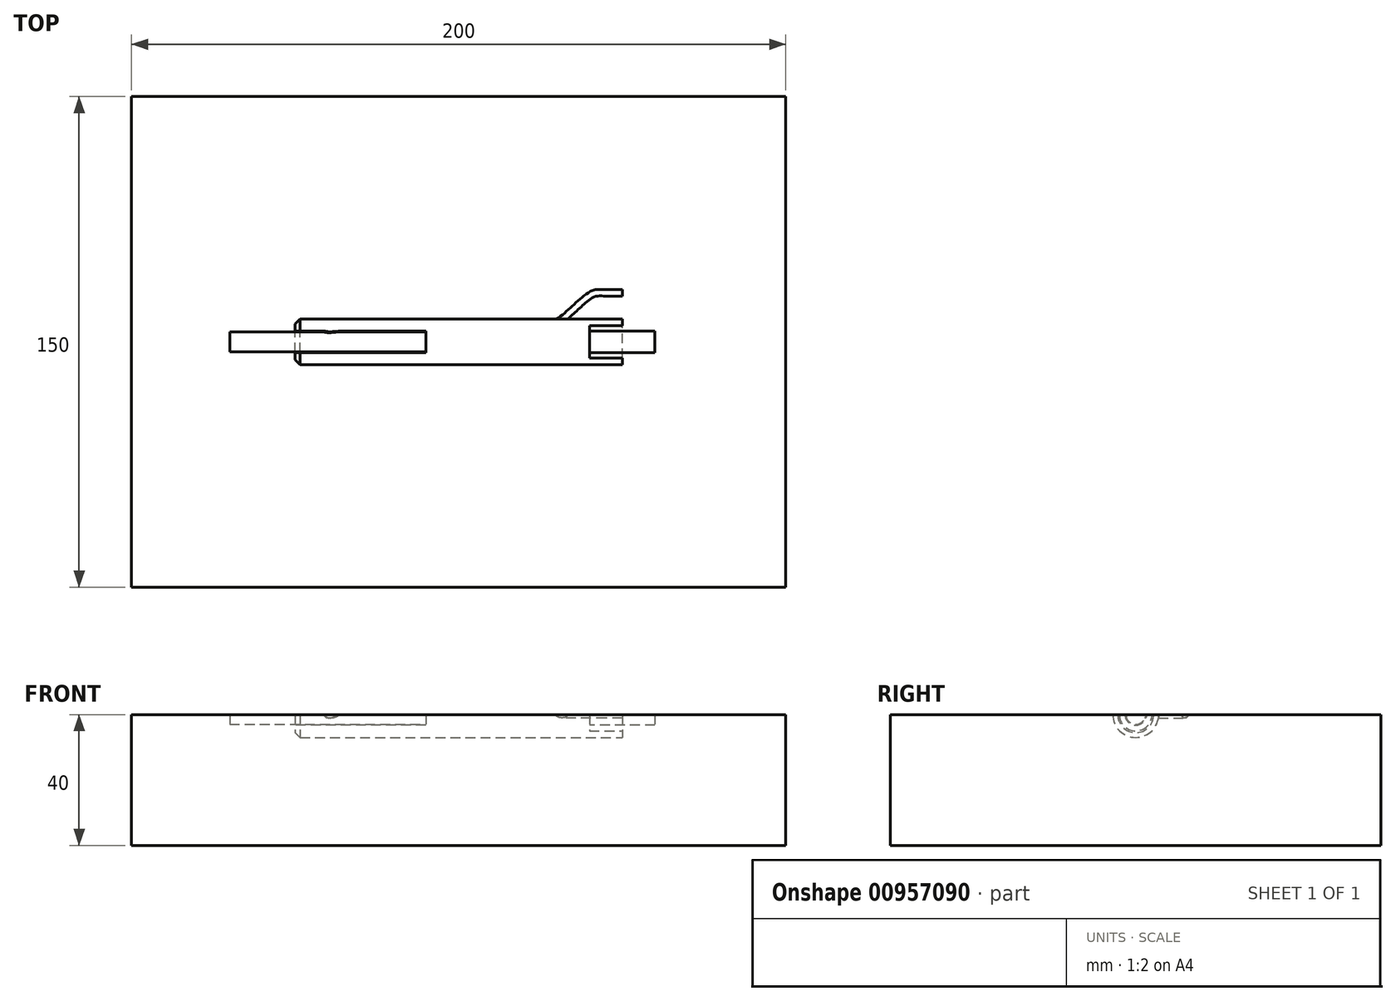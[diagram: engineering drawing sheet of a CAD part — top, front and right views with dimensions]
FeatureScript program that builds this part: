
annotation { "Feature Type Name" : "Feature", "Feature Type Description" : "" }
export const myFeature = defineFeature(function(context is Context, id is Id, definition is map)
    precondition{}
    {
        {
            var Q0;
            Q0=qCreatedBy(makeId("Top.planeOp"),FACE);
            var sketch = newSketch(context, id + "F0", { "sketchPlane" : qUnion([Q0])});
            skLineSegment(sketch, "E0.bottom", {"start": v(-100, 75) * mm, "end": v(100, 75) * mm});
            skLineSegment(sketch, "E0.top", {"start": v(-100, -75) * mm, "end": v(100, -75) * mm});
            skLineSegment(sketch, "E0.left", {"start": v(-100, 75) * mm, "end": v(-100, -75) * mm});
            skLineSegment(sketch, "E0.right", {"start": v(100, 75) * mm, "end": v(100, -75) * mm});
            skSolve(sketch);
        }
        {
            var Q0;
            Q0=makeQuery(id+"F0.imprint","IMPRINT",FACE,{"disambiguationData":[TD([[makeQuery(id+"F0.imprint","IMPRINT",EDGE,{"derivedFrom":sQuery(id+"F0.wireOp",EDGE,"E0.bottom")}),-1.0]])]});
            extrude(context, id + "F1", {"entities" : qUnion([Q0]), "oppositeDirection" : true, "depth" : 40 * mm, "offsetDistance" : 25 * mm});
        }
        {
            var Q0;
            Q0=qCreatedBy(makeId("Right.planeOp"),FACE);
            var sketch = newSketch(context, id + "F2", { "sketchPlane" : qUnion([Q0])});
            skArc(sketch, "E1", {"start": v(-7, 0) * mm, "mid": v(0, -7) * mm, "end": v(7, 0) * mm});
            skLineSegment(sketch, "E2.0.0", {"start": v(75, 0) * mm, "end": v(-75, 0) * mm});
            skLineSegment(sketch, "E2.0.2", {"start": v(-75, 0) * mm, "end": v(75, 0) * mm, "construction": true});
            skLineSegment(sketch, "E3", {"start": v(7, 0) * mm, "end": v(-7, 0) * mm});
            skSolve(sketch);
        }
        {
            var Q0;
            Q0 = qSketchRegion(id + "F2", true);
            extrude(context, id + "F3", {"entities" : qUnion([Q0]), "operationType" : NewBodyOperationType.REMOVE, "endBound" : BoundingType.SYMMETRIC, "oppositeDirection" : true, "depth" : 100 * mm, "offsetDistance" : 25 * mm});
        }
        {
            var Q0;
            Q0=makeQuery(id+"F3.boolean.opBoolean","COPY",FACE,{"derivedFrom":makeQuery(id+"F3.opExtrude","CAP_FACE",FACE,{"disambiguationData":[OSD([sQuery(id+"F2.wireOp",EDGE,"E1"),sQuery(id+"F2.wireOp",EDGE,"E3")])],"isStart":true})});
            var sketch = newSketch(context, id + "F4", { "sketchPlane" : qUnion([Q0])});
            skPoint(sketch, "E4.0", {"position": v(0, 0) * mm});
            skArc(sketch, "E5", {"start": v(-5, 0) * mm, "mid": v(0, -5) * mm, "end": v(5, 0) * mm});
            skLineSegment(sketch, "E6", {"start": v(-5, 0) * mm, "end": v(5, 0) * mm});
            skSolve(sketch);
        }
        {
            var Q0;
            Q0=makeQuery(id+"F4.imprint","IMPRINT",FACE,{"disambiguationData":[TD([[makeQuery(id+"F4.imprint","IMPRINT",EDGE,{"derivedFrom":sQuery(id+"F4.wireOp",EDGE,"E5")}),1.0]])]});
            extrude(context, id + "F5", {"entities" : qUnion([Q0]), "operationType" : NewBodyOperationType.ADD, "depth" : 10 * mm, "offsetDistance" : 25 * mm});
        }
        {
            var Q0;
            Q0=makeQuery(id+"F5.opExtrude","CAP_FACE",FACE,{"disambiguationData":[OSD([sQuery(id+"F4.wireOp",EDGE,"E5"),sQuery(id+"F4.wireOp",EDGE,"E6")])],"isStart":false});
            var sketch = newSketch(context, id + "F6", { "sketchPlane" : qUnion([Q0])});
            skCircle(sketch, "E7", {"center": v(0, 0) * mm, "radius": 3.25 * mm});
            skSolve(sketch);
        }
        {
            var Q0;
            {var subQ0=sQuery(id+"F6.wireOp",EDGE,"E7");var subQ1=makeQuery(id+"F5.opExtrude","CAP_EDGE",EDGE,{"disambiguationData":[OSD([sQuery(id+"F4.wireOp",EDGE,"E6")])],"isStart":false});var subQ2=makeQuery(id+"F6.imprint","INTERSECT",VERTEX,{"disambiguationData":[OD(0.0)],"derivedFrom":[subQ1,subQ0]});Q0=makeQuery(id+"F6.imprint","IMPRINT",FACE,{"disambiguationData":[TD([[makeQuery(id+"F6.imprint","IMPRINT",EDGE,{"disambiguationData":[TD([[subQ2,1.0]])],"derivedFrom":subQ0}),1.0]])]});}
            var Q1;
            {var subQ0=sQuery(id+"F6.wireOp",EDGE,"E7");var subQ1=makeQuery(id+"F5.opExtrude","CAP_EDGE",EDGE,{"disambiguationData":[OSD([sQuery(id+"F4.wireOp",EDGE,"E6")])],"isStart":false});var subQ2=makeQuery(id+"F6.imprint","INTERSECT",VERTEX,{"disambiguationData":[OD(0.0)],"derivedFrom":[subQ1,subQ0]});Q1=makeQuery(id+"F6.imprint","IMPRINT",FACE,{"disambiguationData":[TD([[makeQuery(id+"F6.imprint","IMPRINT",EDGE,{"disambiguationData":[TD([[subQ2,-1.0]])],"derivedFrom":subQ0}),1.0]])]});}
            extrude(context, id + "F7", {"entities" : qUnion([Q0, Q1]), "operationType" : NewBodyOperationType.REMOVE, "oppositeDirection" : true, "depth" : 20 * mm, "offsetDistance" : 25 * mm});
        }
        {
            var Q0;
            Q0=makeQuery(id+"F3.boolean.opBoolean","COPY",FACE,{"derivedFrom":makeQuery(id+"F3.opExtrude","CAP_FACE",FACE,{"disambiguationData":[OSD([sQuery(id+"F2.wireOp",EDGE,"E1"),sQuery(id+"F2.wireOp",EDGE,"E3")])],"isStart":false})});
            var sketch = newSketch(context, id + "F8", { "sketchPlane" : qUnion([Q0])});
            skArc(sketch, "E8", {"start": v(-3.25, 0) * mm, "mid": v(0, -3.25) * mm, "end": v(3.25, 0) * mm});
            skLineSegment(sketch, "E9", {"start": v(-3.25, 0) * mm, "end": v(3.25, 0) * mm});
            skSolve(sketch);
        }
        {
            var Q0;
            Q0 = qSketchRegion(id + "F8", true);
            extrude(context, id + "F9", {"entities" : qUnion([Q0]), "operationType" : NewBodyOperationType.ADD, "depth" : 40 * mm, "offsetDistance" : 25 * mm});
        }
        {
            var Q0;
            Q0=makeQuery(id+"F3.boolean.opBoolean","COPY",EDGE,{"derivedFrom":makeQuery(id+"F3.opExtrude","CAP_EDGE",EDGE,{"disambiguationData":[OSD([sQuery(id+"F2.wireOp",EDGE,"E1")])],"isStart":false})});
            chamfer(context, id + "F10", {"entities" : qUnion([Q0]), "width" : 1.5 * mm, "tangentPropagation" : true});
        }
        {
            var Q0;
            Q0=makeQuery(id+"F1.opExtrude","CAP_FACE",FACE,{"disambiguationData":[OSD([sQuery(id+"F0.wireOp",EDGE,"E0.bottom"),sQuery(id+"F0.wireOp",EDGE,"E0.top"),sQuery(id+"F0.wireOp",EDGE,"E0.left"),sQuery(id+"F0.wireOp",EDGE,"E0.right")])],"isStart":true});
            var sketch = newSketch(context, id + "F11", { "sketchPlane" : qUnion([Q0])});
            skLineSegment(sketch, "E10.0", {"start": v(50, -5) * mm, "end": v(50, -7) * mm});
            skLineSegment(sketch, "E11.0.0", {"start": v(-100, 75) * mm, "end": v(-100, -75) * mm});
            skLineSegment(sketch, "E11.0.1", {"start": v(-100, -75) * mm, "end": v(100, -75) * mm});
            skLineSegment(sketch, "E11.0.2", {"start": v(100, -75) * mm, "end": v(100, 75) * mm});
            skLineSegment(sketch, "E11.0.3", {"start": v(100, 75) * mm, "end": v(-100, 75) * mm});
            skLineSegment(sketch, "E12", {"start": v(50, 15) * mm, "end": v(45, 15) * mm});
            skFitSpline(sketch, "E13", {"points": [v(45, 15) * mm, v(40.7, 14.52) * mm, v(31.65, 7) * mm, v(21.87, 5) * mm, v(-30.52, 5) * mm, v(-43.04, 0) * mm], "startDerivative": vector(-47.27, 0) * mm, "endDerivative": vector(-74.54, -70.61) * mm});
            skLineSegment(sketch, "E14.0.1", {"start": v(50, 7) * mm, "end": v(-50, 7) * mm});
            skLineSegment(sketch, "E14.0.2", {"start": v(-50, -7) * mm, "end": v(-50, 7) * mm});
            skLineSegment(sketch, "E14.0.3", {"start": v(-50, -7) * mm, "end": v(50, -7) * mm});
            skSolve(sketch);
        }
        {
            var Q0;
            Q0=makeQuery(id+"F3.boolean.opBoolean","COPY",FACE,{"derivedFrom":makeQuery(id+"F3.opExtrude","CAP_FACE",FACE,{"disambiguationData":[OSD([sQuery(id+"F2.wireOp",EDGE,"E1"),sQuery(id+"F2.wireOp",EDGE,"E3")])],"isStart":true})});
            var sketch = newSketch(context, id + "F12", { "sketchPlane" : qUnion([Q0])});
            skPoint(sketch, "E15.0", {"position": v(-15, 0) * mm});
            skCircle(sketch, "E16", {"center": v(-15, 0) * mm, "radius": 1 * mm});
            skSolve(sketch);
        }
        {
            var Q0;
            Q0=makeQuery(id+"F12.imprint","IMPRINT",FACE,{"disambiguationData":[TD([[makeQuery(id+"F12.imprint","IMPRINT",EDGE,{"derivedFrom":sQuery(id+"F12.wireOp",EDGE,"E16")}),1.0]])]});
            var Q1;
            Q1=sQuery(id+"F11.wireOp",EDGE,"E12");
            var Q2;
            Q2=sQuery(id+"F11.wireOp",EDGE,"E13");
            sweep(context, id + "F13", {"operationType" : NewBodyOperationType.REMOVE, "profiles" : qUnion([Q0]), "path" : qUnion([Q1, Q2])});
        }
        {
            var Q0;
            Q0=makeQuery(id+"F11.imprint","IMPRINT",FACE,{"disambiguationData":[TD([[makeQuery(id+"F11.imprint","IMPRINT",EDGE,{"derivedFrom":sQuery(id+"F11.wireOp",EDGE,"E11.0.0")}),1.0]])]});
            var sketch = newSketch(context, id + "F14", { "sketchPlane" : qUnion([Q0])});
            skLineSegment(sketch, "E17", {"start": v(79, 0) * mm, "end": v(-86.52, 0) * mm, "construction": true});
            skSolve(sketch);
        }
        {
            var Q0;
            Q0=makeQuery(id+"F9.opExtrude","CAP_FACE",FACE,{"disambiguationData":[OSD([sQuery(id+"F8.wireOp",EDGE,"E8"),sQuery(id+"F8.wireOp",EDGE,"E9")])],"isStart":false});
            var sketch = newSketch(context, id + "F15", { "sketchPlane" : qUnion([Q0])});
            skCircle(sketch, "E18", {"center": v(0, 0) * mm, "radius": 3 * mm});
            skSolve(sketch);
        }
        {
            var Q0;
            {var subQ0=sQuery(id+"F15.wireOp",EDGE,"E18");var subQ1=makeQuery(id+"F9.opExtrude","CAP_EDGE",EDGE,{"disambiguationData":[OSD([sQuery(id+"F8.wireOp",EDGE,"E9")])],"isStart":false});var subQ2=makeQuery(id+"F15.imprint","INTERSECT",VERTEX,{"disambiguationData":[OD(0.0)],"derivedFrom":[subQ1,subQ0]});Q0=makeQuery(id+"F15.imprint","IMPRINT",FACE,{"disambiguationData":[TD([[makeQuery(id+"F15.imprint","IMPRINT",EDGE,{"disambiguationData":[TD([[subQ2,-1.0]])],"derivedFrom":subQ0}),1.0]])]});}
            extrude(context, id + "F16", {"entities" : qUnion([Q0]), "operationType" : NewBodyOperationType.REMOVE, "oppositeDirection" : true, "depth" : 60 * mm, "offsetDistance" : 25 * mm});
        }
    });
